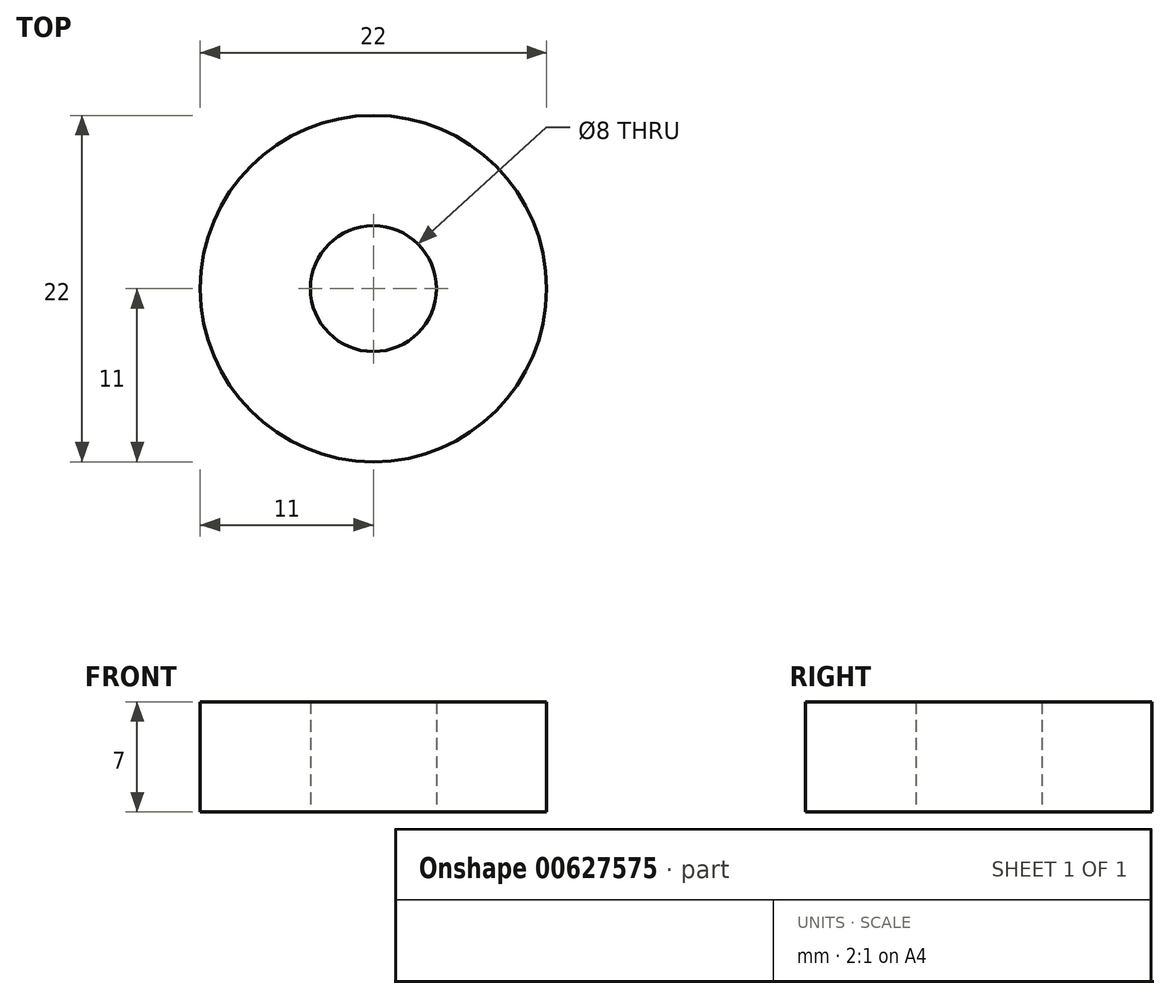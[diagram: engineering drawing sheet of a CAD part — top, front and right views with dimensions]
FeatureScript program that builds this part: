
annotation { "Feature Type Name" : "Feature", "Feature Type Description" : "" }
export const myFeature = defineFeature(function(context is Context, id is Id, definition is map)
    precondition{}
    {
        {
            var Q0;
            Q0=qCreatedBy(makeId("Top.planeOp"),FACE);
            var sketch = newSketch(context, id + "F0", { "sketchPlane" : qUnion([Q0])});
            skCircle(sketch, "E0", {"center": v(0, 0) * mm, "radius": 11 * mm});
            skCircle(sketch, "E1", {"center": v(0, 0) * mm, "radius": 4 * mm});
            skSolve(sketch);
        }
        {
            var Q0;
            Q0 = qSketchRegion(id + "F0", true);
            var Q1;
            Q1=makeQuery(id+"F0.imprint","IMPRINT",FACE,{"disambiguationData":[TD([[makeQuery(id+"F0.imprint","IMPRINT",EDGE,{"derivedFrom":sQuery(id+"F0.wireOp",EDGE,"E0")}),1.0]])]});
            var Q2;
            Q2=sQuery(id+"F0.wireOp",EDGE,"E0");
            var Q3;
            Q3=sQuery(id+"F0.wireOp",EDGE,"E1");
            extrude(context, id + "F1", {"entities" : qUnion([Q0, Q1]), "surfaceEntities" : qUnion([Q2, Q3]), "depth" : 7 * mm, "offsetDistance" : 25 * mm});
        }
    });
